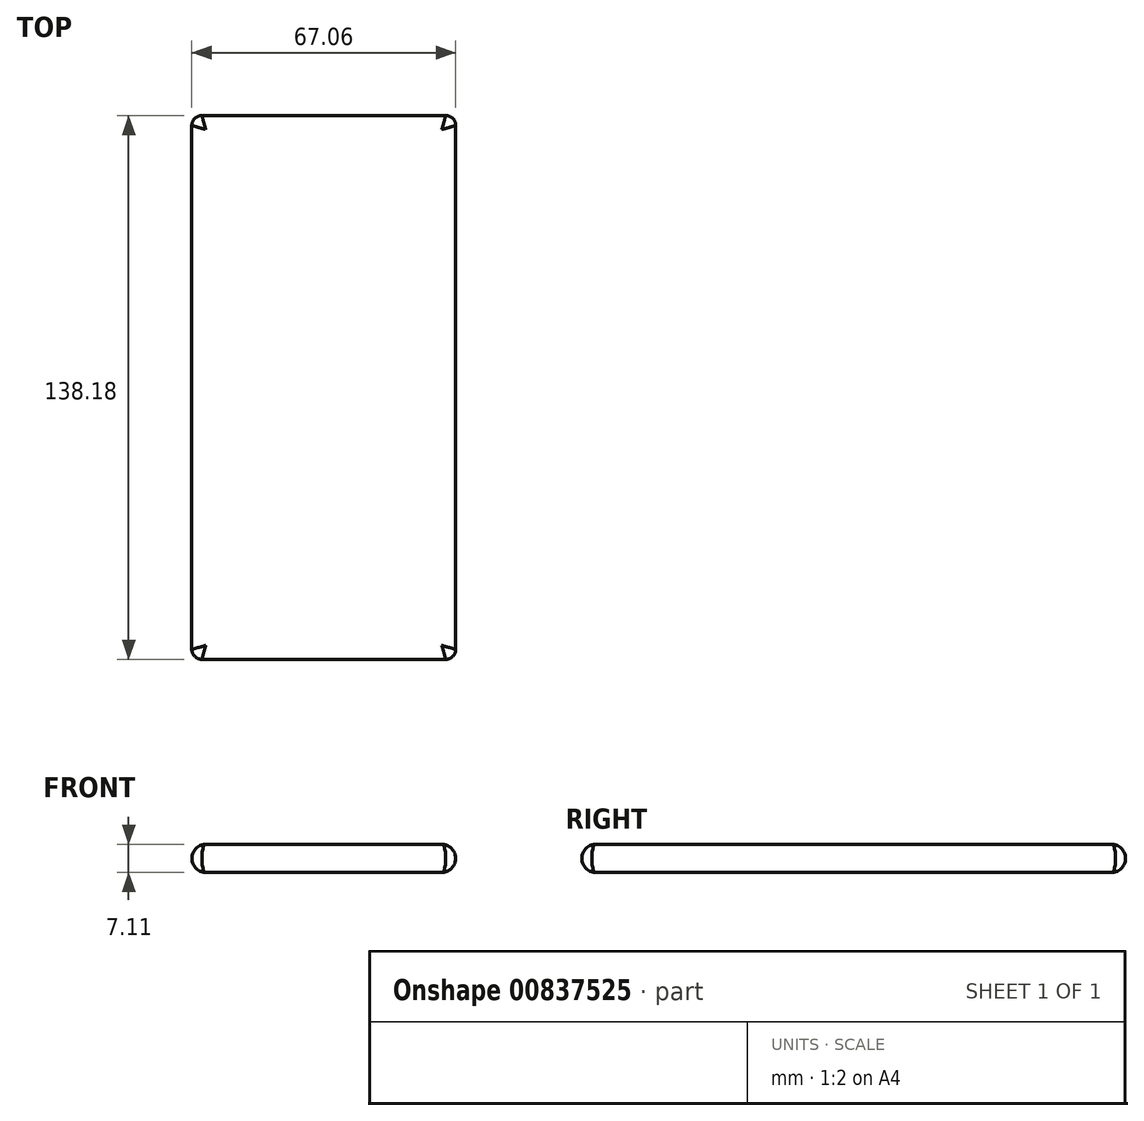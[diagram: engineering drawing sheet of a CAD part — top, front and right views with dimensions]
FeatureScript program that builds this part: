
annotation { "Feature Type Name" : "Feature", "Feature Type Description" : "" }
export const myFeature = defineFeature(function(context is Context, id is Id, definition is map)
    precondition{}
    {
        {
            var Q0;
            Q0=qCreatedBy(makeId("Top.planeOp"),FACE);
            var sketch = newSketch(context, id + "F0", { "sketchPlane" : qUnion([Q0])});
            skLineSegment(sketch, "E0.bottom", {"start": v(-49.77, 63.24) * mm, "end": v(17.29, 63.24) * mm});
            skLineSegment(sketch, "E0.top", {"start": v(-49.77, -74.94) * mm, "end": v(17.29, -74.94) * mm});
            skLineSegment(sketch, "E0.left", {"start": v(-49.77, 63.24) * mm, "end": v(-49.77, -74.94) * mm});
            skLineSegment(sketch, "E0.right", {"start": v(17.29, 63.24) * mm, "end": v(17.29, -74.94) * mm});
            skSolve(sketch);
        }
        {
            var Q0;
            Q0 = qSketchRegion(id + "F0", true);
            var Q1;
            Q1=makeQuery(id+"F0.imprint","IMPRINT",FACE,{"disambiguationData":[TD([[makeQuery(id+"F0.imprint","IMPRINT",EDGE,{"derivedFrom":sQuery(id+"F0.wireOp",EDGE,"E0.bottom")}),-1.0]])]});
            extrude(context, id + "F1", {"entities" : qUnion([Q0, Q1]), "depth" : 7.11 * mm, "offsetDistance" : 25.4 * mm});
        }
        {
            var Q0;
            Q0=makeQuery(id+"F1.opExtrude","CAP_EDGE",EDGE,{"disambiguationData":[OSD([sQuery(id+"F0.wireOp",EDGE,"E0.bottom")])],"isStart":false});
            var Q1;
            Q1=makeQuery(id+"F1.opExtrude","CAP_EDGE",EDGE,{"disambiguationData":[OSD([sQuery(id+"F0.wireOp",EDGE,"E0.bottom")])],"isStart":true});
            var Q2;
            Q2=makeQuery(id+"F1.opExtrude","CAP_EDGE",EDGE,{"disambiguationData":[OSD([sQuery(id+"F0.wireOp",EDGE,"E0.right")])],"isStart":true});
            var Q3;
            Q3=makeQuery(id+"F1.opExtrude","CAP_EDGE",EDGE,{"disambiguationData":[OSD([sQuery(id+"F0.wireOp",EDGE,"E0.right")])],"isStart":false});
            var Q4;
            Q4=makeQuery(id+"F1.opExtrude","CAP_EDGE",EDGE,{"disambiguationData":[OSD([sQuery(id+"F0.wireOp",EDGE,"E0.top")])],"isStart":false});
            var Q5;
            Q5=makeQuery(id+"F1.opExtrude","CAP_EDGE",EDGE,{"disambiguationData":[OSD([sQuery(id+"F0.wireOp",EDGE,"E0.top")])],"isStart":true});
            var Q6;
            Q6=makeQuery(id+"F1.opExtrude","CAP_EDGE",EDGE,{"disambiguationData":[OSD([sQuery(id+"F0.wireOp",EDGE,"E0.left")])],"isStart":true});
            var Q7;
            Q7=makeQuery(id+"F1.opExtrude","CAP_EDGE",EDGE,{"disambiguationData":[OSD([sQuery(id+"F0.wireOp",EDGE,"E0.left")])],"isStart":false});
            fillet(context, id + "F2", {"entities" : qUnion([Q0, Q1, Q2, Q3, Q4, Q5, Q6, Q7]), "radius" : 3.56 * mm, "tangentPropagation" : true, "allowEdgeOverflow" : false});
        }
        {
            var Q0;
            Q0=makeQuery(id+"F2.opFillet","BLEND_EDGE",EDGE,{"blendedFrom":[makeQuery(id+"F1.opExtrude","CAP_EDGE",EDGE,{"disambiguationData":[OSD([sQuery(id+"F0.wireOp",EDGE,"E0.top")])],"isStart":true}),makeQuery(id+"F1.opExtrude","CAP_EDGE",EDGE,{"disambiguationData":[OSD([sQuery(id+"F0.wireOp",EDGE,"E0.left")])],"isStart":true})],"blendedInto":[]});
            var Q1;
            Q1=makeQuery(id+"F2.opFillet","BLEND_EDGE",EDGE,{"blendedFrom":[makeQuery(id+"F1.opExtrude","CAP_EDGE",EDGE,{"disambiguationData":[OSD([sQuery(id+"F0.wireOp",EDGE,"E0.top")])],"isStart":true}),makeQuery(id+"F1.opExtrude","CAP_EDGE",EDGE,{"disambiguationData":[OSD([sQuery(id+"F0.wireOp",EDGE,"E0.right")])],"isStart":true})],"blendedInto":[]});
            var Q2;
            Q2=makeQuery(id+"F2.opFillet","BLEND_EDGE",EDGE,{"blendedFrom":[makeQuery(id+"F1.opExtrude","CAP_EDGE",EDGE,{"disambiguationData":[OSD([sQuery(id+"F0.wireOp",EDGE,"E0.bottom")])],"isStart":true}),makeQuery(id+"F1.opExtrude","CAP_EDGE",EDGE,{"disambiguationData":[OSD([sQuery(id+"F0.wireOp",EDGE,"E0.right")])],"isStart":true})],"blendedInto":[]});
            var Q3;
            Q3=makeQuery(id+"F2.opFillet","BLEND_EDGE",EDGE,{"blendedFrom":[makeQuery(id+"F1.opExtrude","CAP_EDGE",EDGE,{"disambiguationData":[OSD([sQuery(id+"F0.wireOp",EDGE,"E0.bottom")])],"isStart":true}),makeQuery(id+"F1.opExtrude","CAP_EDGE",EDGE,{"disambiguationData":[OSD([sQuery(id+"F0.wireOp",EDGE,"E0.left")])],"isStart":true})],"blendedInto":[]});
            fillet(context, id + "F3", {"entities" : qUnion([Q0, Q1, Q2, Q3]), "radius" : 2.54 * mm, "allowEdgeOverflow" : false});
        }
    });
